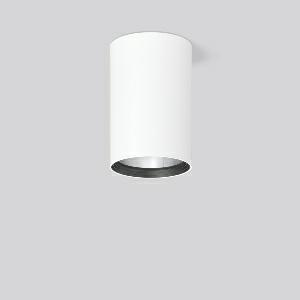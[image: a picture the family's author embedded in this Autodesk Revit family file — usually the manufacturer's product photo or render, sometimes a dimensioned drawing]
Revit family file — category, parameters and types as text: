
# Revit family: heledon_maxi_a_931237_002_76_63c5
name_source: partatom
category: Lighting Fixtures
units: mm (PartAtom-declared; Revit-internal decimal feet)

## family parameters
Cut with Voids When Loaded = No
Host = Face
Light Source = No
Part Type = Normal
Room Calculation Point = No
Round Connector Dimension = Use Diameter
Shared = No

## types (1)
- HELEDON maxi A (1 x LED Modul 920 meat+, 2200 lm, 2000)
    Apparent Load = 33 VA
    Approval mark = CE
    CIE Flux Codes = 100 100 100 100 100
    Color Rendering = 90
    Color Temperature = 2000
    Default Elevation = 1800 mm
    Description = Series: HELEDON maxi
Cylindrical surface-mounted downlight. Housing: die-cast aluminium, powder-coated. Internal ceiling frame polycarbonate with bayonet mounting. Black plastic ring and recessed LED to prevent glare from the side. Optical assembly with reflector made of MIRO-Silver with 98% total light reflection for outstanding efficiency - can be changed without tools. Special LED for illumination of meat included. Suitable for Ceiling mounting. Easy installation with a separate ceiling frame with bayonet mounting and plug connection. Driver integrated. Connected via plug-in connector. High quality converter without flickering and stroboscopic effect. The following accessories can be mounted without use of tools: interchangeable lenses, decorative glasses, honeycomb louvre, clear and frosted diffusers, white interchangeable plastic ring. 
Colour: traffic white, matt (RAL 9016)
Diameter: 123 mm
Height: 183 mm
Lamp: LED
Socket: without socket
Colour temperature: meat +
System power: 33 W
Rated luminous flux: 2200 lm
Luminous efficiency: 67 lm/W
Control gear: Converter, dimmable, DALI
Protection class: I
Type of protection: IP 20
    Height = 183 mm
    Lamp = 1 x LED Modul 920 meat+
    Lamp Light Flux = 2200 lm
    Lamp count = 1
    Length = 123 mm
    Lifetime = 50000 h
    Luminous efficacy = 67 lm/W
    Manufacturer = RZB
    ModVariant = No
    Model = 931237.002.76
    Mounting Place = Ceiling
    Mounting Type = Surface mounted
    Number of Poles = 1
    OnlyDefault = Yes
    Power Factor = 1
    Product Name = HELEDON maxi A
    Product group = Surface mounted downlights
    ProductGroupID = 302
    Protection Class = Protection class I
    Protection Degree = IP 20
    RLX_Detail_Level = 1
    RLX_Emergency_Light_Flux = 0 lm
    RLX_Emergency_Type = 0
    RLX_Emergency_Type_DB = No
    RlxData = <blob elided: 98113 chars, md5=6fd27c6a>
    Socket = socket
    Standby Power = 0 W
    System Light Flux = 2200 lm
    System Power = 33 W
    Type Comments = Product without accessories
    Type Image = 931192.002.jpg
    URL = http://relux.com
    VarID = ---
    Voltage = 230 V
    Voltage Range = 220-240 V
    Weight = 0.00 kg
    Width = 0 mm  [stored 0 ft]

note: [stored X ft] marks values corroborated as IEEE doubles in the binary element streams (Revit-internal decimal feet)

## geometry (parser evidence)
native form markers: Blend x4, Sweep x12
no freeform markers — native parametric forms only
